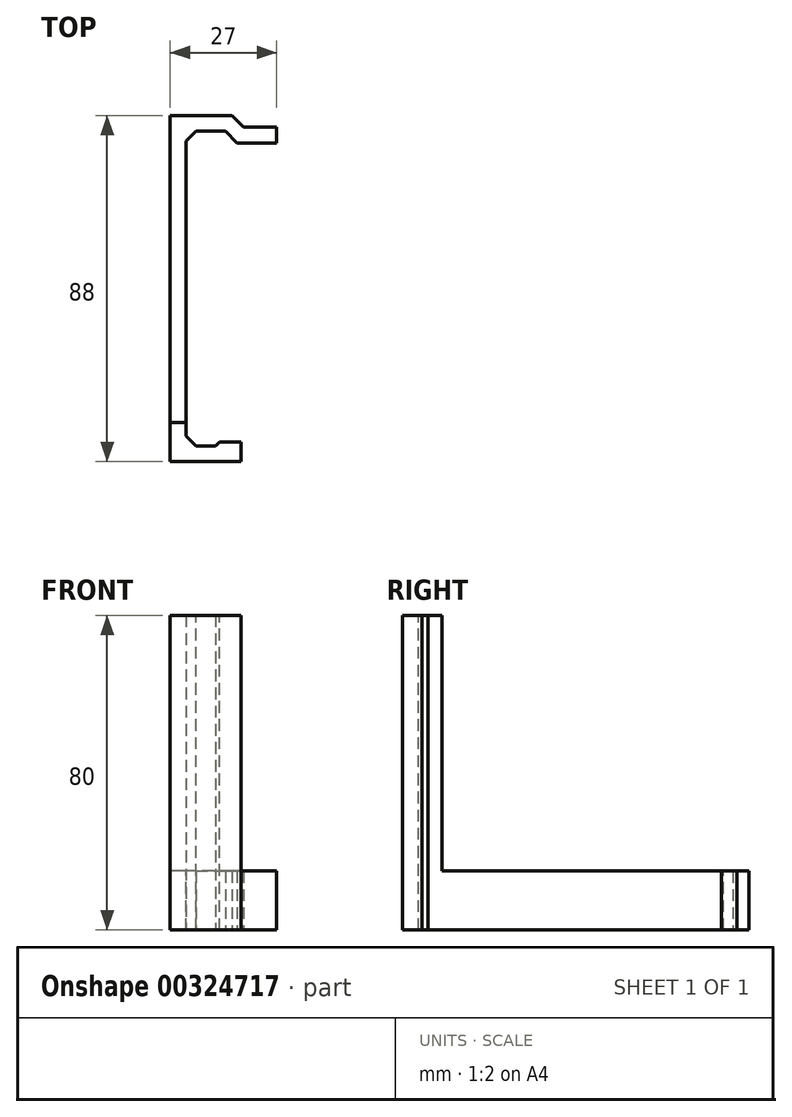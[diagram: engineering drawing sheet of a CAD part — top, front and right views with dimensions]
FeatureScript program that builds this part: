
annotation { "Feature Type Name" : "Feature", "Feature Type Description" : "" }
export const myFeature = defineFeature(function(context is Context, id is Id, definition is map)
    precondition{}
    {
        {
            var Q0;
            Q0=qCreatedBy(makeId("Top.planeOp"),FACE);
            var sketch = newSketch(context, id + "F0", { "sketchPlane" : qUnion([Q0])});
            skLineSegment(sketch, "E0", {"start": v(0, 0) * mm, "end": v(18, 0) * mm});
            skLineSegment(sketch, "E1", {"start": v(4, 4) * mm, "end": v(4, 84) * mm});
            skLineSegment(sketch, "E2", {"start": v(4, 84) * mm, "end": v(14, 84) * mm});
            skLineSegment(sketch, "E3", {"start": v(14, 84) * mm, "end": v(17, 81) * mm});
            skLineSegment(sketch, "E4", {"start": v(17, 81) * mm, "end": v(27, 81) * mm});
            skLineSegment(sketch, "E5", {"start": v(27, 81) * mm, "end": v(27, 85) * mm});
            skLineSegment(sketch, "E6", {"start": v(27, 85) * mm, "end": v(18.66, 85) * mm});
            skLineSegment(sketch, "E7", {"start": v(18.66, 85) * mm, "end": v(15.66, 88) * mm});
            skLineSegment(sketch, "E8", {"start": v(15.66, 88) * mm, "end": v(0, 88) * mm});
            skLineSegment(sketch, "E9", {"start": v(0, 88) * mm, "end": v(0, 0) * mm});
            skLineSegment(sketch, "E10", {"start": v(14, 4) * mm, "end": v(14, 5) * mm});
            skLineSegment(sketch, "E11", {"start": v(14, 5) * mm, "end": v(18, 5) * mm});
            skLineSegment(sketch, "E12.trimOffspring", {"start": v(14, 4) * mm, "end": v(4, 4) * mm});
            skLineSegment(sketch, "E13", {"start": v(18, 5) * mm, "end": v(18, 0) * mm});
            skSolve(sketch);
        }
        {
            var Q0;
            Q0=makeQuery(id+"F0.imprint","IMPRINT",FACE,{"disambiguationData":[TD([[makeQuery(id+"F0.imprint","IMPRINT",EDGE,{"derivedFrom":sQuery(id+"F0.wireOp",EDGE,"E0")}),1.0]])]});
            extrude(context, id + "F1", {"entities" : qUnion([Q0]), "depth" : 15 * mm});
        }
        {
            var Q0;
            Q0=makeQuery(id+"F1.opExtrude","CAP_FACE",FACE,{"disambiguationData":[OSD([sQuery(id+"F0.wireOp",EDGE,"E0"),sQuery(id+"F0.wireOp",EDGE,"SYVxu5xy-XV6r-TBil-cyuT-aJpqpxVzzVMq"),sQuery(id+"F0.wireOp",EDGE,"92TtqJ47-xHCl-4OPv-Nny3-ELrVnvgCmDDr"),sQuery(id+"F0.wireOp",EDGE,"E1"),sQuery(id+"F0.wireOp",EDGE,"E2"),sQuery(id+"F0.wireOp",EDGE,"E3"),sQuery(id+"F0.wireOp",EDGE,"E4"),sQuery(id+"F0.wireOp",EDGE,"E5"),sQuery(id+"F0.wireOp",EDGE,"E6"),sQuery(id+"F0.wireOp",EDGE,"E7"),sQuery(id+"F0.wireOp",EDGE,"E8"),sQuery(id+"F0.wireOp",EDGE,"E9"),sQuery(id+"F0.wireOp",EDGE,"E10"),sQuery(id+"F0.wireOp",EDGE,"E11"),sQuery(id+"F0.wireOp",EDGE,"B9QAjMfU-C6dN-mIht-A4zd-EJnB9D8HX5yY"),sQuery(id+"F0.wireOp",EDGE,"E12.trimOffspring")])],"isStart":false});
            var sketch = newSketch(context, id + "F2", { "sketchPlane" : qUnion([Q0])});
            skLineSegment(sketch, "E14.0.4", {"start": v(0, 10) * mm, "end": v(0, 0) * mm});
            skLineSegment(sketch, "E14.0.12", {"start": v(4, 4) * mm, "end": v(4, 10) * mm});
            skLineSegment(sketch, "E15", {"start": v(4, 10) * mm, "end": v(0, 10) * mm});
            skPoint(sketch, "E16.orphan", {"position": v(4, 84) * mm});
            skPoint(sketch, "E17.orphan", {"position": v(0, 88) * mm});
            skLineSegment(sketch, "E18.0", {"start": v(14, 4) * mm, "end": v(4, 4) * mm});
            skLineSegment(sketch, "E19.0", {"start": v(0, 0) * mm, "end": v(18, 0) * mm});
            skLineSegment(sketch, "E20.0", {"start": v(14, 5) * mm, "end": v(18, 5) * mm});
            skLineSegment(sketch, "E21.0", {"start": v(14, 4) * mm, "end": v(14, 5) * mm});
            skLineSegment(sketch, "E22.0", {"start": v(18, 5) * mm, "end": v(18, 0) * mm});
            skSolve(sketch);
        }
        {
            var Q0;
            Q0 = qSketchRegion(id + "F2", true);
            extrude(context, id + "F3", {"entities" : qUnion([Q0]), "operationType" : NewBodyOperationType.ADD, "depth" : 65 * mm});
        }
        {
            var Q0;
            Q0=makeQuery(id+"F1.opExtrude","SWEPT_EDGE",EDGE,{"disambiguationData":[OSD([sQuery(id+"F0.wireOp",EDGE,"E1"),sQuery(id+"F0.wireOp",EDGE,"E2")])]});
            var Q1;
            Q1=makeQuery(id+"F3.boolean.opBoolean","MERGE",EDGE,{"derivedFrom":[makeQuery(id+"F1.opExtrude","SWEPT_EDGE",EDGE,{"disambiguationData":[OSD([sQuery(id+"F0.wireOp",EDGE,"E1"),sQuery(id+"F0.wireOp",EDGE,"E12.trimOffspring")])]}),makeQuery(id+"F3.opExtrude","SWEPT_EDGE",EDGE,{"disambiguationData":[OSD([sQuery(id+"F2.wireOp",EDGE,"E14.0.11"),sQuery(id+"F2.wireOp",EDGE,"E14.0.12")])]})]});
            var Q2;
            Q2=makeQuery(id+"F3.boolean.opBoolean","MERGE",EDGE,{"derivedFrom":[makeQuery(id+"F1.opExtrude","SWEPT_EDGE",EDGE,{"disambiguationData":[OSD([sQuery(id+"F0.wireOp",EDGE,"E10"),sQuery(id+"F0.wireOp",EDGE,"E12.trimOffspring")])]}),makeQuery(id+"F3.opExtrude","SWEPT_EDGE",EDGE,{"disambiguationData":[OSD([sQuery(id+"F2.wireOp",EDGE,"E14.0.10"),sQuery(id+"F2.wireOp",EDGE,"E14.0.11")])]})]});
            var Q3;
            Q3=makeQuery(id+"F3.boolean.opBoolean","MERGE",EDGE,{"derivedFrom":[makeQuery(id+"F1.opExtrude","SWEPT_EDGE",EDGE,{"disambiguationData":[OSD([sQuery(id+"F0.wireOp",EDGE,"92TtqJ47-xHCl-4OPv-Nny3-ELrVnvgCmDDr"),sQuery(id+"F0.wireOp",EDGE,"B9QAjMfU-C6dN-mIht-A4zd-EJnB9D8HX5yY")])]}),makeQuery(id+"F3.opExtrude","SWEPT_EDGE",EDGE,{"disambiguationData":[OSD([sQuery(id+"F2.wireOp",EDGE,"E14.0.7"),sQuery(id+"F2.wireOp",EDGE,"E14.0.8")])]})]});
            chamfer(context, id + "F4", {"entities" : qUnion([Q0, Q1, Q2, Q3]), "width" : 2.5 * mm, "tangentPropagation" : true});
        }
    });
